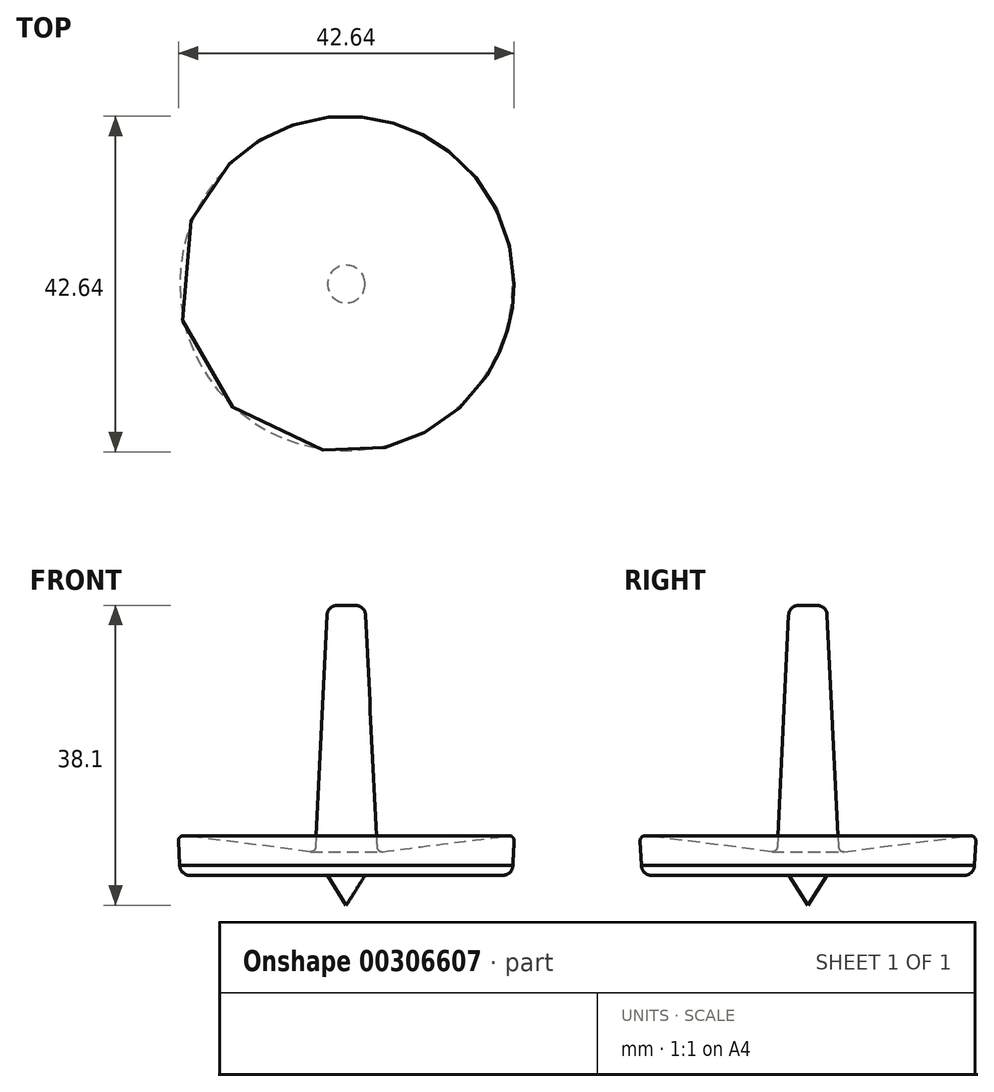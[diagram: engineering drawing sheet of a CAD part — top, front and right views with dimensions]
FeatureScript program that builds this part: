
annotation { "Feature Type Name" : "Feature", "Feature Type Description" : "" }
export const myFeature = defineFeature(function(context is Context, id is Id, definition is map)
    precondition{}
    {
        {
            var Q0;
            Q0=qCreatedBy(makeId("Front.planeOp"),FACE);
            var sketch = newSketch(context, id + "F0", { "sketchPlane" : qUnion([Q0])});
            skLineSegment(sketch, "E0", {"start": v(0, 0) * mm, "end": v(0, 38.1) * mm, "construction": true});
            skLineSegment(sketch, "E1", {"start": v(0, 38.1) * mm, "end": v(1.18, 38.1) * mm});
            skLineSegment(sketch, "E2", {"start": v(2.45, 36.9) * mm, "end": v(3.63, 12.77) * mm});
            skLineSegment(sketch, "E3", {"start": v(19.89, 3.81) * mm, "end": v(2.39, 3.81) * mm});
            skLineSegment(sketch, "E4", {"start": v(2.39, 3.81) * mm, "end": v(0, 0) * mm});
            skPoint(sketch, "E5.visualSharp", {"position": v(3.92, 6.73) * mm});
            skPoint(sketch, "E6.visualSharp", {"position": v(2.39, 38.1) * mm});
            skArc(sketch, "E6.filletArc", {"start": v(2.45, 36.9) * mm, "mid": v(2.05, 37.75) * mm, "end": v(1.18, 38.1) * mm});
            skPoint(sketch, "E7.visualSharp", {"position": v(21.44, 3.81) * mm});
            skArc(sketch, "E7.filletArc", {"start": v(19.89, 3.81) * mm, "mid": v(20.77, 4.17) * mm, "end": v(21.16, 5.04) * mm});
            skLineSegment(sketch, "E8", {"start": v(0, 38.1) * mm, "end": v(0, 0) * mm});
            skLineSegment(sketch, "E9", {"start": v(3.63, 12.77) * mm, "end": v(3.89, 7.41) * mm});
            skLineSegment(sketch, "E10", {"start": v(4.6, 6.81) * mm, "end": v(20.6, 8.83) * mm});
            skLineSegment(sketch, "E11", {"start": v(21.32, 8.17) * mm, "end": v(21.16, 5.04) * mm});
            skPoint(sketch, "E12.visualSharp", {"position": v(21.35, 8.93) * mm});
            skArc(sketch, "E12.filletArc", {"start": v(21.32, 8.17) * mm, "mid": v(21.11, 8.67) * mm, "end": v(20.6, 8.83) * mm});
            skArc(sketch, "E13.filletArc", {"start": v(3.89, 7.41) * mm, "mid": v(4.11, 6.96) * mm, "end": v(4.6, 6.81) * mm});
            skSolve(sketch);
        }
        {
            var Q0;
            Q0 = qSketchRegion(id + "F0", true);
            var Q1;
            Q1=sQuery(id+"F0.wireOp",EDGE,"E8");
            revolve(context, id + "F1", {"entities" : qUnion([Q0]), "axis" : qUnion([Q1]), "revolveType" : RevolveType.FULL});
        }
    });
